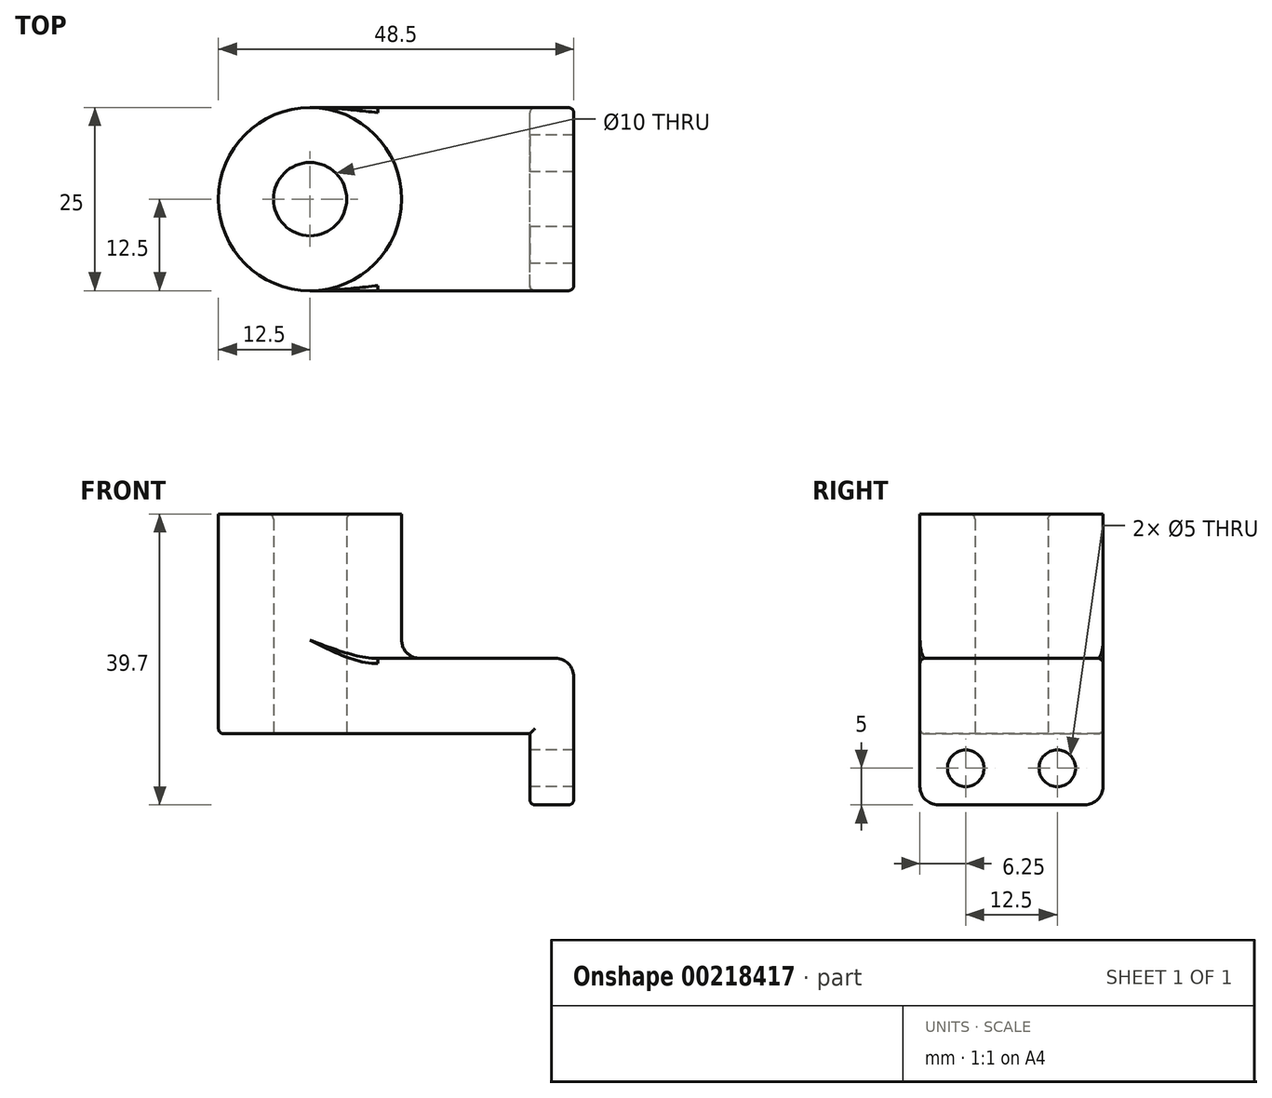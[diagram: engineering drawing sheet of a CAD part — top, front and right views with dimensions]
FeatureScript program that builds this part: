
annotation { "Feature Type Name" : "Feature", "Feature Type Description" : "" }
export const myFeature = defineFeature(function(context is Context, id is Id, definition is map)
    precondition{}
    {
        {
            var Q0;
            Q0=qCreatedBy(makeId("Top.planeOp"),FACE);
            var sketch = newSketch(context, id + "F0", { "sketchPlane" : qUnion([Q0])});
            skLineSegment(sketch, "E0.bottom", {"start": v(-15, -12.5) * mm, "end": v(15, -12.5) * mm});
            skLineSegment(sketch, "E0.top", {"start": v(-15, 12.5) * mm, "end": v(15, 12.5) * mm});
            skLineSegment(sketch, "E0.left", {"start": v(-15, -12.5) * mm, "end": v(-15, 12.5) * mm});
            skLineSegment(sketch, "E0.right", {"start": v(15, -12.5) * mm, "end": v(15, 12.5) * mm});
            skPoint(sketch, "E0.middle", {"position": v(0, 0) * mm});
            skCircle(sketch, "E1", {"center": v(-15, 0) * mm, "radius": 12.5 * mm});
            skCircle(sketch, "E2", {"center": v(-15, 0) * mm, "radius": 5 * mm});
            skSolve(sketch);
        }
        {
            var Q0;
            {var subQ0=sQuery(id+"F0.wireOp",EDGE,"E0.bottom");Q0=makeQuery(id+"F0.imprint","IMPRINT",FACE,{"disambiguationData":[TD([[makeQuery(id+"F0.imprint","IMPRINT",EDGE,{"derivedFrom":subQ0}),1.0]])]});}
            var Q1;
            {var subQ1=sQuery(id+"F0.wireOp",EDGE,"E0.left");var subQ3=sQuery(id+"F0.wireOp",EDGE,"E2");var subQ4=makeQuery(id+"F0.imprint","INTERSECT",VERTEX,{"disambiguationData":[OD(0.0)],"derivedFrom":[subQ1,subQ3]});Q1=makeQuery(id+"F0.imprint","IMPRINT",FACE,{"disambiguationData":[TD([[makeQuery(id+"F0.imprint","IMPRINT",EDGE,{"disambiguationData":[TD([[subQ4,1.0]])],"derivedFrom":subQ3}),-1.0]])]});}
            var Q2;
            {var subQ0=sQuery(id+"F0.wireOp",EDGE,"E2");var subQ1=sQuery(id+"F0.wireOp",EDGE,"E0.left");var subQ2=makeQuery(id+"F0.imprint","INTERSECT",VERTEX,{"disambiguationData":[OD(0.0)],"derivedFrom":[subQ1,subQ0]});Q2=makeQuery(id+"F0.imprint","IMPRINT",FACE,{"disambiguationData":[TD([[makeQuery(id+"F0.imprint","IMPRINT",EDGE,{"disambiguationData":[TD([[subQ2,-1.0]])],"derivedFrom":subQ1}),1.0]])]});}
            var Q3;
            {var subQ0=sQuery(id+"F0.wireOp",EDGE,"E2");var subQ1=sQuery(id+"F0.wireOp",EDGE,"E0.left");var subQ2=makeQuery(id+"F0.imprint","INTERSECT",VERTEX,{"disambiguationData":[OD(0.0)],"derivedFrom":[subQ1,subQ0]});Q3=makeQuery(id+"F0.imprint","IMPRINT",FACE,{"disambiguationData":[TD([[makeQuery(id+"F0.imprint","IMPRINT",EDGE,{"disambiguationData":[TD([[subQ2,-1.0]])],"derivedFrom":subQ1}),-1.0]])]});}
            var Q4;
            {var subQ1=sQuery(id+"F0.wireOp",EDGE,"E0.left");var subQ3=sQuery(id+"F0.wireOp",EDGE,"E2");var subQ4=makeQuery(id+"F0.imprint","INTERSECT",VERTEX,{"disambiguationData":[OD(0.0)],"derivedFrom":[subQ1,subQ3]});Q4=makeQuery(id+"F0.imprint","IMPRINT",FACE,{"disambiguationData":[TD([[makeQuery(id+"F0.imprint","IMPRINT",EDGE,{"disambiguationData":[TD([[subQ4,-1.0]])],"derivedFrom":subQ3}),-1.0]])]});}
            extrude(context, id + "F1", {"entities" : qUnion([Q0, Q1, Q2, Q3, Q4]), "depth" : 10.3 * mm});
        }
        {
            var Q0;
            {var subQ1=sQuery(id+"F0.wireOp",EDGE,"E0.left");var subQ3=sQuery(id+"F0.wireOp",EDGE,"E2");var subQ4=makeQuery(id+"F0.imprint","INTERSECT",VERTEX,{"disambiguationData":[OD(0.0)],"derivedFrom":[subQ1,subQ3]});Q0=makeQuery(id+"F0.imprint","IMPRINT",FACE,{"disambiguationData":[TD([[makeQuery(id+"F0.imprint","IMPRINT",EDGE,{"disambiguationData":[TD([[subQ4,1.0]])],"derivedFrom":subQ3}),-1.0]])]});}
            var Q1;
            {var subQ1=sQuery(id+"F0.wireOp",EDGE,"E0.left");var subQ3=sQuery(id+"F0.wireOp",EDGE,"E2");var subQ4=makeQuery(id+"F0.imprint","INTERSECT",VERTEX,{"disambiguationData":[OD(0.0)],"derivedFrom":[subQ1,subQ3]});Q1=makeQuery(id+"F0.imprint","IMPRINT",FACE,{"disambiguationData":[TD([[makeQuery(id+"F0.imprint","IMPRINT",EDGE,{"disambiguationData":[TD([[subQ4,-1.0]])],"derivedFrom":subQ3}),-1.0]])]});}
            extrude(context, id + "F2", {"entities" : qUnion([Q0, Q1]), "operationType" : NewBodyOperationType.ADD, "depth" : 30 * mm});
        }
        {
            var Q0;
            Q0=makeQuery(id+"F1.opExtrude","SWEPT_FACE",FACE,{"disambiguationData":[OSD([sQuery(id+"F0.wireOp",EDGE,"E0.right")])]});
            var sketch = newSketch(context, id + "F3", { "sketchPlane" : qUnion([Q0])});
            skLineSegment(sketch, "E3.bottom", {"start": v(-12.5, 10.3) * mm, "end": v(12.5, 10.3) * mm});
            skLineSegment(sketch, "E3.top", {"start": v(-12.5, -9.7) * mm, "end": v(12.5, -9.7) * mm});
            skLineSegment(sketch, "E3.left", {"start": v(-12.5, 10.3) * mm, "end": v(-12.5, -9.7) * mm});
            skLineSegment(sketch, "E3.right", {"start": v(12.5, 10.3) * mm, "end": v(12.5, -9.7) * mm});
            skCircle(sketch, "E4", {"center": v(-6.25, -4.7) * mm, "radius": 2.5 * mm});
            skLineSegment(sketch, "E5", {"start": v(0, -0.6) * mm, "end": v(0, -9.7) * mm, "construction": true});
            skPoint(sketch, "E5.startSnap0", {"position": v(0, 0) * mm});
            skLineSegment(sketch, "E6", {"start": v(0, -9.7) * mm, "end": v(0, 0) * mm, "construction": true});
            skCircle(sketch, "E7.MirrorC", {"center": v(6.25, -4.7) * mm, "radius": 2.5 * mm});
            skSolve(sketch);
        }
        {
            var Q0;
            {var subQ0=sQuery(id+"F3.wireOp",EDGE,"E3.bottom");Q0=makeQuery(id+"F3.imprint","IMPRINT",FACE,{"disambiguationData":[TD([[makeQuery(id+"F3.imprint","IMPRINT",EDGE,{"derivedFrom":subQ0}),-1.0]])]});}
            var Q1;
            {var subQ0=sQuery(id+"F3.wireOp",EDGE,"E3.top");Q1=makeQuery(id+"F3.imprint","IMPRINT",FACE,{"disambiguationData":[TD([[makeQuery(id+"F3.imprint","IMPRINT",EDGE,{"derivedFrom":subQ0}),1.0]])]});}
            extrude(context, id + "F4", {"entities" : qUnion([Q0, Q1]), "operationType" : NewBodyOperationType.ADD, "depth" : 6 * mm});
        }
        {
            var Q0;
            Q0=makeQuery(id+"F4.opExtrude","CAP_EDGE",EDGE,{"disambiguationData":[OSD([sQuery(id+"F3.wireOp",EDGE,"E3.bottom")])],"isStart":false});
            var Q1;
            {var subQ0=sQuery(id+"F0.wireOp",EDGE,"E1");Q1=makeQuery(id+"F2.boolean.opBoolean","INTERSECT",EDGE,{"derivedFrom":[makeQuery(id+"F1.opExtrude","CAP_FACE",FACE,{"disambiguationData":[OSD([sQuery(id+"F0.wireOp",EDGE,"E0.bottom"),sQuery(id+"F0.wireOp",EDGE,"E0.top"),sQuery(id+"F0.wireOp",EDGE,"E0.right"),subQ0])],"isStart":false}),makeQuery(id+"F2.opExtrude","SWEPT_FACE",FACE,{"disambiguationData":[OSD([subQ0])]})]});}
            var Q2;
            Q2=makeQuery(id+"F4.opExtrude","SWEPT_EDGE",EDGE,{"disambiguationData":[OSD([sQuery(id+"F3.wireOp",EDGE,"E3.top"),sQuery(id+"F3.wireOp",EDGE,"E3.left")])]});
            var Q3;
            Q3=makeQuery(id+"F4.opExtrude","SWEPT_EDGE",EDGE,{"disambiguationData":[OSD([sQuery(id+"F3.wireOp",EDGE,"E3.top"),sQuery(id+"F3.wireOp",EDGE,"E3.right")])]});
            fillet(context, id + "F5", {"entities" : qUnion([Q0, Q1, Q2, Q3]), "radius" : 2.5 * mm, "tangentPropagation" : true, "allowEdgeOverflow" : false});
        }
        {
            var Q0;
            Q0=makeQuery(id+"F1.opExtrude","CAP_EDGE",EDGE,{"disambiguationData":[OSD([sQuery(id+"F0.wireOp",EDGE,"E0.top")])],"isStart":true});
            var Q1;
            Q1=makeQuery(id+"F1.opExtrude","CAP_EDGE",EDGE,{"disambiguationData":[OSD([sQuery(id+"F0.wireOp",EDGE,"E0.top")])],"isStart":false});
            var Q2;
            Q2=makeQuery(id+"F2.opExtrude","CAP_EDGE",EDGE,{"disambiguationData":[OSD([sQuery(id+"F0.wireOp",EDGE,"E2")])],"isStart":false});
            var Q3;
            Q3=makeQuery(id+"F4.opExtrude","CAP_EDGE",EDGE,{"disambiguationData":[OSD([sQuery(id+"F3.wireOp",EDGE,"E3.top")])],"isStart":true});
            fillet(context, id + "F6", {"entities" : qUnion([Q0, Q1, Q2, Q3]), "radius" : 0.7 * mm, "tangentPropagation" : true, "allowEdgeOverflow" : false});
        }
    });
